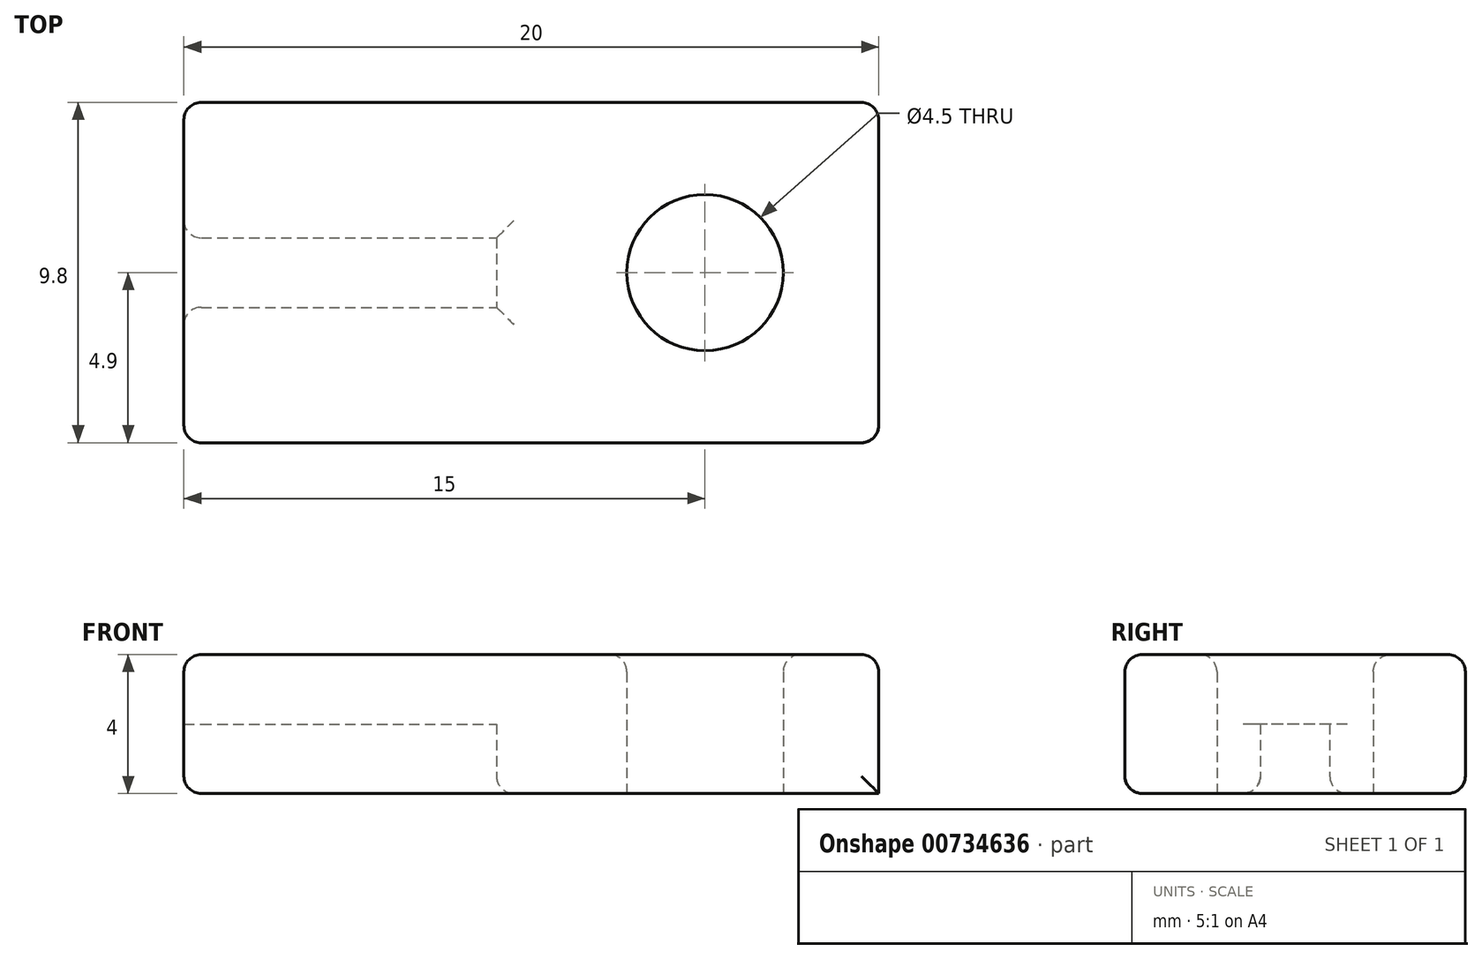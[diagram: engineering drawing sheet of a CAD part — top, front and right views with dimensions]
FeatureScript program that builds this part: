
annotation { "Feature Type Name" : "Feature", "Feature Type Description" : "" }
export const myFeature = defineFeature(function(context is Context, id is Id, definition is map)
    precondition{}
    {
        {
            var Q0;
            Q0=qCreatedBy(makeId("Top.planeOp"),FACE);
            var sketch = newSketch(context, id + "F0", { "sketchPlane" : qUnion([Q0])});
            skLineSegment(sketch, "E0.bottom", {"start": v(20, 9.8) * mm, "end": v(0, 9.8) * mm});
            skLineSegment(sketch, "E0.top", {"start": v(20, 0) * mm, "end": v(0, 0) * mm});
            skLineSegment(sketch, "E0.left", {"start": v(20, 9.8) * mm, "end": v(20, 0) * mm});
            skLineSegment(sketch, "E0.right", {"start": v(0, 9.8) * mm, "end": v(0, 6.4) * mm});
            skLineSegment(sketch, "E1.bottom", {"start": v(0.5, 5.9) * mm, "end": v(9, 5.9) * mm});
            skLineSegment(sketch, "E1.top", {"start": v(0.5, 3.9) * mm, "end": v(9, 3.9) * mm});
            skLineSegment(sketch, "E1.right", {"start": v(9, 5.9) * mm, "end": v(9, 3.9) * mm});
            skLineSegment(sketch, "E2.trimOffspring", {"start": v(0, 3.4) * mm, "end": v(0, 0) * mm});
            skPoint(sketch, "E3.visualSharp", {"position": v(0, 5.9) * mm});
            skArc(sketch, "E3.filletArc", {"start": v(0, 6.4) * mm, "mid": v(0.15, 6.05) * mm, "end": v(0.5, 5.9) * mm});
            skPoint(sketch, "E4.visualSharp", {"position": v(0, 3.9) * mm});
            skArc(sketch, "E4.filletArc", {"start": v(0.5, 3.9) * mm, "mid": v(0.15, 3.75) * mm, "end": v(0, 3.4) * mm});
            skCircle(sketch, "E5", {"center": v(15, 4.9) * mm, "radius": 2.25 * mm});
            skSolve(sketch);
        }
        {
            var Q0;
            Q0 = qSketchRegion(id + "F0", true);
            extrude(context, id + "F1", {"entities" : qUnion([Q0]), "depth" : 4 * mm, "offsetDistance" : 25 * mm});
        }
        {
            var Q0;
            Q0=makeQuery(id+"F1.opExtrude","CAP_FACE",FACE,{"disambiguationData":[OSD([sQuery(id+"F0.wireOp",EDGE,"E0.bottom"),sQuery(id+"F0.wireOp",EDGE,"E0.top"),sQuery(id+"F0.wireOp",EDGE,"E0.left"),sQuery(id+"F0.wireOp",EDGE,"E0.right"),sQuery(id+"F0.wireOp",EDGE,"E1.bottom"),sQuery(id+"F0.wireOp",EDGE,"E1.top"),sQuery(id+"F0.wireOp",EDGE,"E1.right"),sQuery(id+"F0.wireOp",EDGE,"E2.trimOffspring"),sQuery(id+"F0.wireOp",EDGE,"E3.filletArc"),sQuery(id+"F0.wireOp",EDGE,"E4.filletArc"),sQuery(id+"F0.wireOp",EDGE,"E5")])],"isStart":false});
            var sketch = newSketch(context, id + "F2", { "sketchPlane" : qUnion([Q0])});
            skLineSegment(sketch, "E6.bottom", {"start": v(0, 6.4) * mm, "end": v(9, 6.4) * mm});
            skLineSegment(sketch, "E6.top", {"start": v(0, 3.4) * mm, "end": v(9, 3.4) * mm});
            skLineSegment(sketch, "E6.left", {"start": v(0, 6.4) * mm, "end": v(0, 3.4) * mm});
            skLineSegment(sketch, "E6.right", {"start": v(9, 6.4) * mm, "end": v(9, 3.4) * mm});
            skSolve(sketch);
        }
        {
            var Q0;
            Q0 = qSketchRegion(id + "F2", true);
            extrude(context, id + "F3", {"entities" : qUnion([Q0]), "operationType" : NewBodyOperationType.ADD, "oppositeDirection" : true, "depth" : 2 * mm, "offsetDistance" : 25 * mm});
        }
        {
            var Q0;
            Q0=makeQuery(id+"F3.boolean.opBoolean","MERGE",FACE,{"derivedFrom":[makeQuery(id+"F1.opExtrude","CAP_FACE",FACE,{"disambiguationData":[OSD([sQuery(id+"F0.wireOp",EDGE,"E0.bottom"),sQuery(id+"F0.wireOp",EDGE,"E0.top"),sQuery(id+"F0.wireOp",EDGE,"E0.left"),sQuery(id+"F0.wireOp",EDGE,"E0.right"),sQuery(id+"F0.wireOp",EDGE,"E1.bottom"),sQuery(id+"F0.wireOp",EDGE,"E1.top"),sQuery(id+"F0.wireOp",EDGE,"E1.right"),sQuery(id+"F0.wireOp",EDGE,"E2.trimOffspring"),sQuery(id+"F0.wireOp",EDGE,"E3.filletArc"),sQuery(id+"F0.wireOp",EDGE,"E4.filletArc"),sQuery(id+"F0.wireOp",EDGE,"E5")])],"isStart":false}),makeQuery(id+"F3.opExtrude","CAP_FACE",FACE,{"disambiguationData":[OSD([sQuery(id+"F2.wireOp",EDGE,"E6.bottom"),sQuery(id+"F2.wireOp",EDGE,"E6.top"),sQuery(id+"F2.wireOp",EDGE,"E6.left"),sQuery(id+"F2.wireOp",EDGE,"E6.right")])],"isStart":true})]});
            var Q1;
            Q1=makeQuery(id+"F1.opExtrude","SWEPT_FACE",FACE,{"disambiguationData":[OSD([sQuery(id+"F0.wireOp",EDGE,"E0.bottom")])]});
            var Q2;
            Q2=makeQuery(id+"F1.opExtrude","SWEPT_FACE",FACE,{"disambiguationData":[OSD([sQuery(id+"F0.wireOp",EDGE,"E0.top")])]});
            fillet(context, id + "F4", {"entities" : qUnion([Q0, Q1, Q2]), "radius" : .5 * mm, "tangentPropagation" : true, "allowEdgeOverflow" : false});
        }
        {
            var Q0;
            Q0=makeQuery(id+"F1.opExtrude","CAP_EDGE",EDGE,{"disambiguationData":[OSD([sQuery(id+"F0.wireOp",EDGE,"E1.bottom")])],"isStart":true});
            var Q1;
            Q1=makeQuery(id+"F1.opExtrude","CAP_EDGE",EDGE,{"disambiguationData":[OSD([sQuery(id+"F0.wireOp",EDGE,"E1.top")])],"isStart":true});
            var Q2;
            Q2=makeQuery(id+"F1.opExtrude","CAP_EDGE",EDGE,{"disambiguationData":[OSD([sQuery(id+"F0.wireOp",EDGE,"E1.right")])],"isStart":true});
            fillet(context, id + "F5", {"entities" : qUnion([Q0, Q1, Q2]), "tangentPropagation" : true, "radius" : 0.5 * mm, "defaultsChanged" : false, "vertexSettings" : [], "allowEdgeOverflow" : false});
        }
    });
